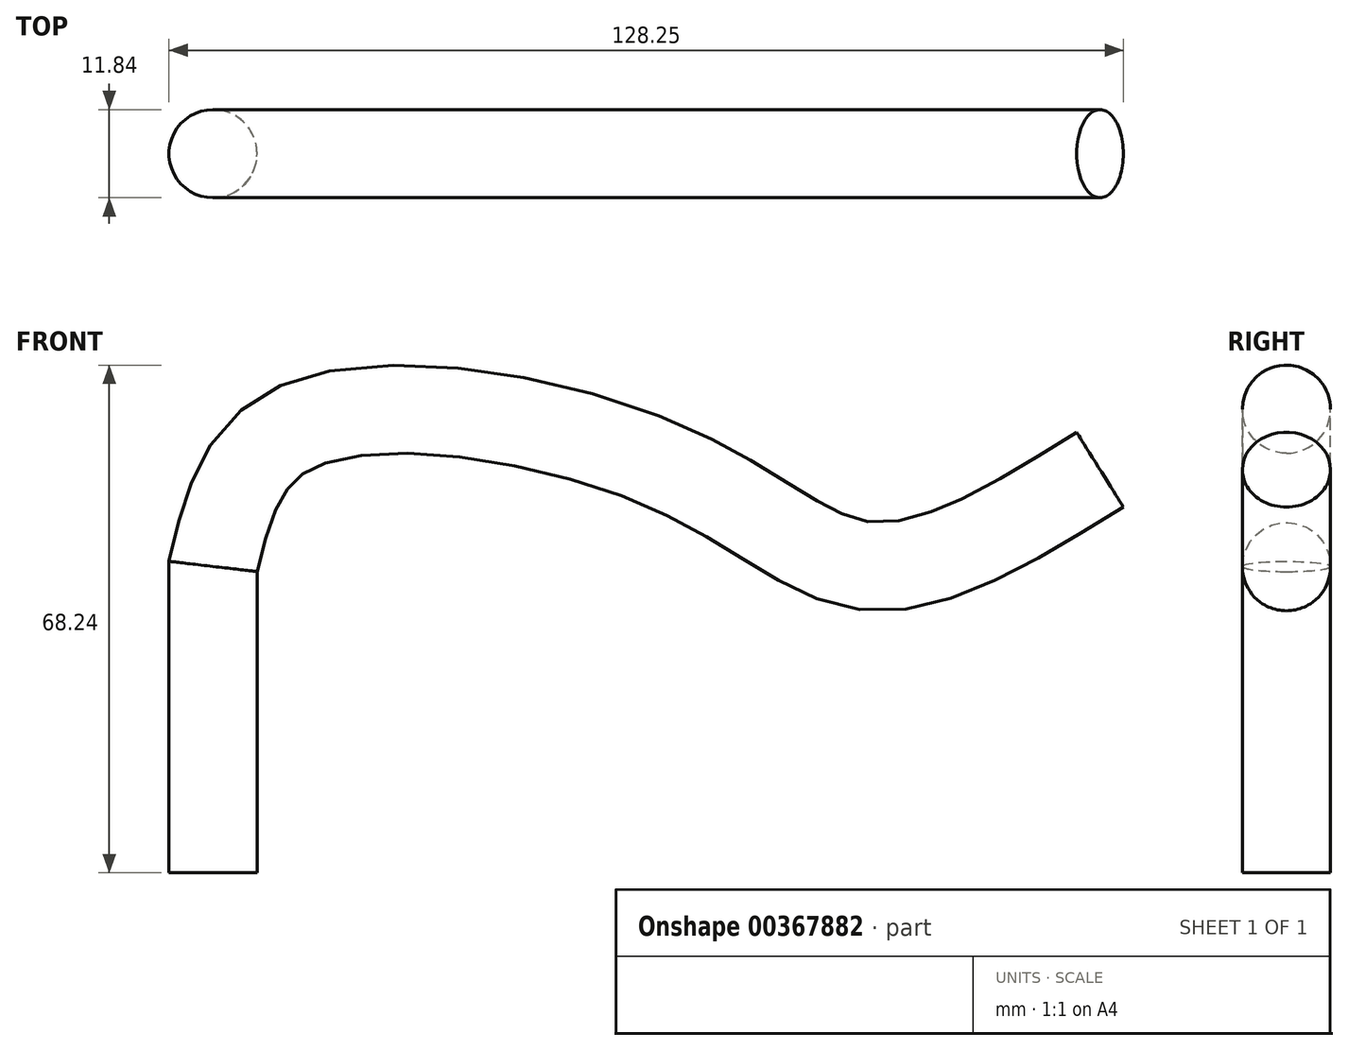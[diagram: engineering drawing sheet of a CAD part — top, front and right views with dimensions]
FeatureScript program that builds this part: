
annotation { "Feature Type Name" : "Feature", "Feature Type Description" : "" }
export const myFeature = defineFeature(function(context is Context, id is Id, definition is map)
    precondition{}
    {
        {
            var Q0;
            Q0=qCreatedBy(makeId("Top.planeOp"),FACE);
            var sketch = newSketch(context, id + "F0", { "sketchPlane" : qUnion([Q0])});
            skCircle(sketch, "E0", {"center": v(0, 0) * mm, "radius": 5.92 * mm});
            skSolve(sketch);
        }
        {
            var Q0;
            Q0=qCreatedBy(makeId("Front.planeOp"),FACE);
            var sketch = newSketch(context, id + "F1", { "sketchPlane" : qUnion([Q0])});
            skLineSegment(sketch, "E1", {"start": v(0, 0) * mm, "end": v(0, 41.18) * mm});
            skFitSpline(sketch, "E2", {"points": [v(0, 41.18) * mm, v(10.84, 59.75) * mm, v(61.92, 54.18) * mm, v(88.55, 41.18) * mm, v(119.2, 54.18) * mm], "startDerivative": vector(26.48, 111.92) * mm, "endDerivative": vector(130.4, 81.28) * mm});
            skSolve(sketch);
        }
        {
            var Q0;
            Q0=makeQuery(id+"F0.imprint","IMPRINT",FACE,{"disambiguationData":[TD([[makeQuery(id+"F0.imprint","IMPRINT",EDGE,{"derivedFrom":sQuery(id+"F0.wireOp",EDGE,"E0")}),1.0]])]});
            var Q1;
            Q1=sQuery(id+"F1.wireOp",EDGE,"E1");
            var Q2;
            Q2=sQuery(id+"F1.wireOp",EDGE,"E2");
            sweep(context, id + "F2", {"profiles" : qUnion([Q0]), "path" : qUnion([Q1, Q2])});
        }
    });
